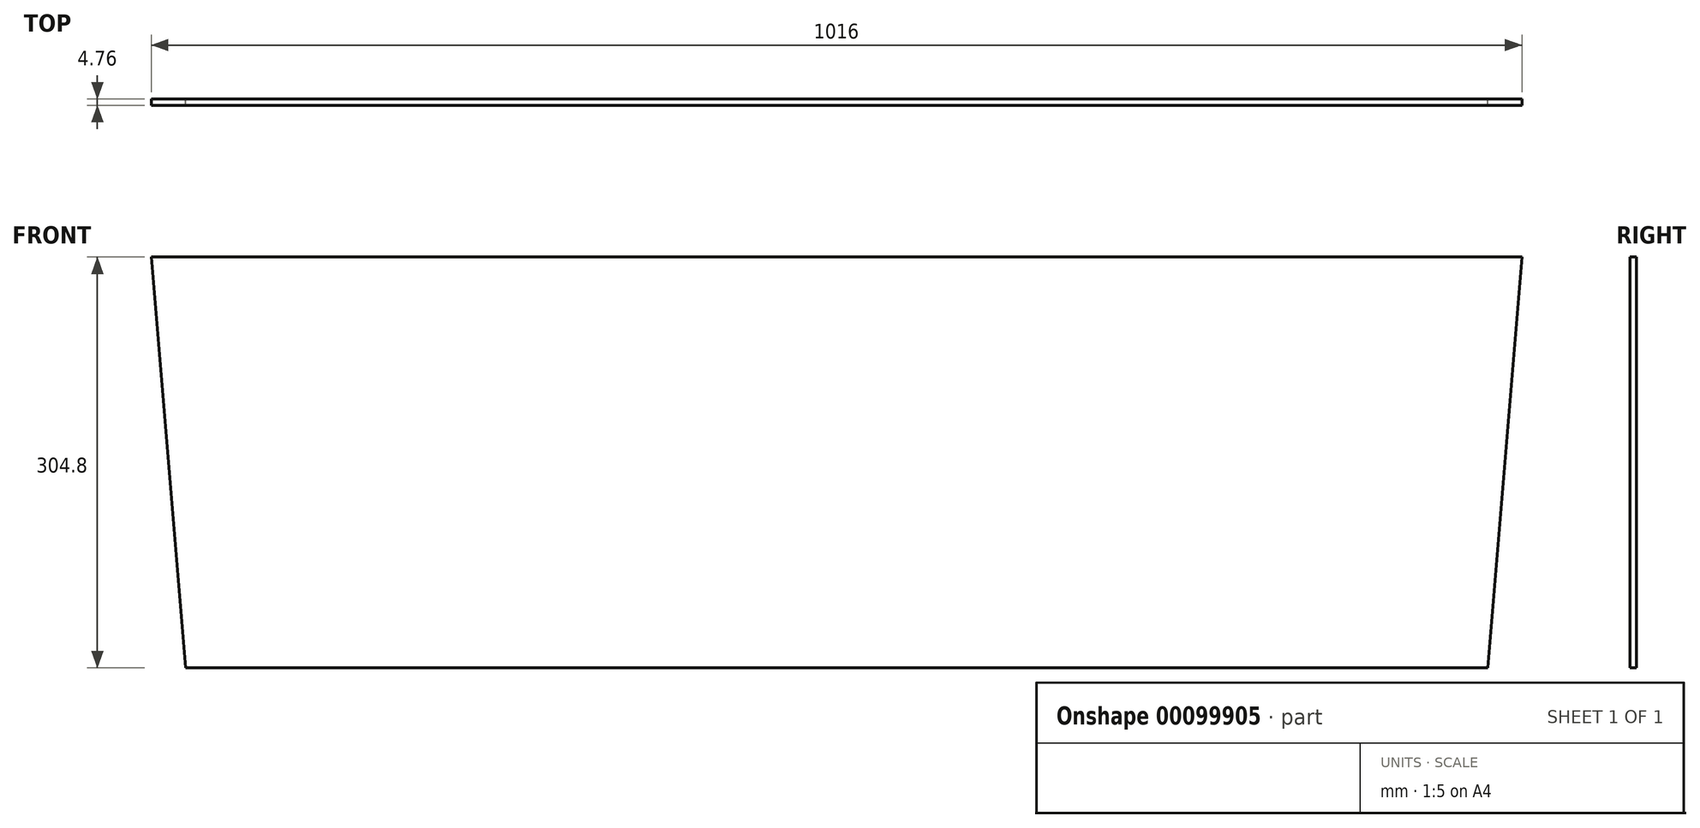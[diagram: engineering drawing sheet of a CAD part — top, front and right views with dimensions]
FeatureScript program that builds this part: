
annotation { "Feature Type Name" : "Feature", "Feature Type Description" : "" }
export const myFeature = defineFeature(function(context is Context, id is Id, definition is map)
    precondition{}
    {
        {
            var Q0;
            Q0=qCreatedBy(makeId("Front.planeOp"),FACE);
            var sketch = newSketch(context, id + "F0", { "sketchPlane" : qUnion([Q0])});
            skLineSegment(sketch, "E0.bottom", {"start": v(-337.4, 33.66) * mm, "end": v(323, 33.66) * mm});
            skLineSegment(sketch, "E0.top", {"start": v(-337.4, -271.14) * mm, "end": v(627.8, -271.14) * mm});
            skLineSegment(sketch, "E1", {"start": v(-337.4, -271.14) * mm, "end": v(-362.8, 33.66) * mm});
            skLineSegment(sketch, "E2", {"start": v(-362.8, 33.66) * mm, "end": v(-337.4, 33.66) * mm});
            skLineSegment(sketch, "E3", {"start": v(627.8, -271.14) * mm, "end": v(653.2, 33.66) * mm});
            skLineSegment(sketch, "E4", {"start": v(653.2, 33.66) * mm, "end": v(323, 33.66) * mm});
            skSolve(sketch);
        }
        {
            var Q0;
            Q0 = qSketchRegion(id + "F0", true);
            extrude(context, id + "F1", {"entities" : qUnion([Q0]), "depth" : 4.76 * mm});
        }
    });
